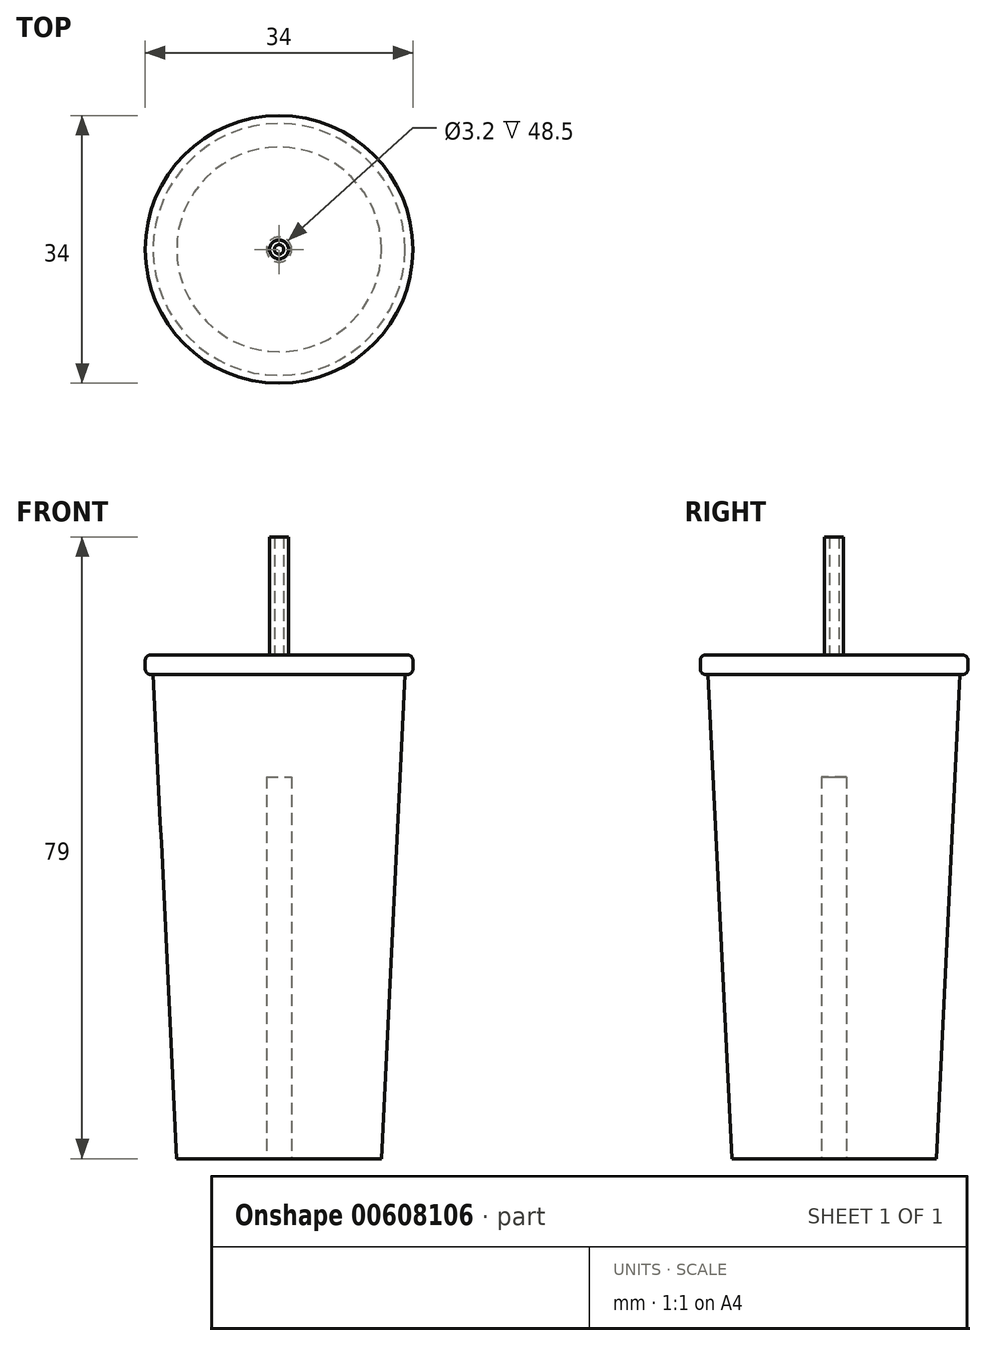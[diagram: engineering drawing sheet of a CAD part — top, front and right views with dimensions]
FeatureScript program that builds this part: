
annotation { "Feature Type Name" : "Feature", "Feature Type Description" : "" }
export const myFeature = defineFeature(function(context is Context, id is Id, definition is map)
    precondition{}
    {
        {
            var Q0;
            Q0=qCreatedBy(makeId("Front.planeOp"),FACE);
            var sketch = newSketch(context, id + "F0", { "sketchPlane" : qUnion([Q0])});
            skLineSegment(sketch, "E0", {"start": v(0, 0) * mm, "end": v(13, 0) * mm});
            skLineSegment(sketch, "E1", {"start": v(0, 0) * mm, "end": v(0, 61.5) * mm});
            skLineSegment(sketch, "E2", {"start": v(0, 61.5) * mm, "end": v(16, 61.5) * mm});
            skLineSegment(sketch, "E3", {"start": v(16, 61.5) * mm, "end": v(13, 0) * mm});
            skLineSegment(sketch, "E4", {"start": v(0, 61.5) * mm, "end": v(0, 64) * mm});
            skLineSegment(sketch, "E5", {"start": v(0, 64) * mm, "end": v(16.3, 64) * mm});
            skLineSegment(sketch, "E6", {"start": v(17, 63.3) * mm, "end": v(17, 62.2) * mm});
            skLineSegment(sketch, "E7", {"start": v(16.3, 61.5) * mm, "end": v(16, 61.5) * mm});
            skPoint(sketch, "E8.visualSharp", {"position": v(17, 64) * mm});
            skArc(sketch, "E8.filletArc", {"start": v(17, 63.3) * mm, "mid": v(16.8, 63.8) * mm, "end": v(16.3, 64) * mm});
            skPoint(sketch, "E9.visualSharp", {"position": v(17, 61.5) * mm});
            skArc(sketch, "E9.filletArc", {"start": v(16.3, 61.5) * mm, "mid": v(16.8, 61.7) * mm, "end": v(17, 62.2) * mm});
            skLineSegment(sketch, "E10", {"start": v(0, 64) * mm, "end": v(0, 79) * mm, "construction": true});
            skLineSegment(sketch, "E11", {"start": v(0, 79) * mm, "end": v(0.6, 79) * mm, "construction": true});
            skLineSegment(sketch, "E12", {"start": v(0.6, 79) * mm, "end": v(0.6, 64) * mm});
            skLineSegment(sketch, "E13", {"start": v(0.6, 79) * mm, "end": v(1.2, 79) * mm});
            skLineSegment(sketch, "E14", {"start": v(1.2, 79) * mm, "end": v(1.2, 64) * mm});
            skSolve(sketch);
        }
        {
            var Q0;
            {var subQ0=sQuery(id+"F0.wireOp",EDGE,"E12");Q0=makeQuery(id+"F0.imprint","IMPRINT",FACE,{"disambiguationData":[TD([[makeQuery(id+"F0.imprint","IMPRINT",EDGE,{"derivedFrom":subQ0}),1.0]])]});}
            var Q1;
            Q1=makeQuery(id+"F0.imprint","IMPRINT",FACE,{"disambiguationData":[TD([[makeQuery(id+"F0.imprint","IMPRINT",EDGE,{"derivedFrom":sQuery(id+"F0.wireOp",EDGE,"E2")}),1.0]])]});
            var Q2;
            Q2=makeQuery(id+"F0.imprint","IMPRINT",FACE,{"disambiguationData":[TD([[makeQuery(id+"F0.imprint","IMPRINT",EDGE,{"derivedFrom":sQuery(id+"F0.wireOp",EDGE,"E0")}),1.0]])]});
            var Q3;
            Q3=sQuery(id+"F0.wireOp",EDGE,"E10");
            revolve(context, id + "F1", {"entities" : qUnion([Q0, Q1, Q2]), "axis" : qUnion([Q3]), "revolveType" : RevolveType.FULL});
        }
        {
            var Q0;
            Q0=makeQuery(id+"F1.opRevolve","SWEPT_FACE",FACE,{"disambiguationData":[OSD([sQuery(id+"F0.wireOp",EDGE,"E0")])]});
            var sketch = newSketch(context, id + "F2", { "sketchPlane" : qUnion([Q0])});
            skCircle(sketch, "E15", {"center": v(0, 0) * mm, "radius": 1.6 * mm});
            skSolve(sketch);
        }
        {
            var Q0;
            Q0=makeQuery(id+"F2.imprint","IMPRINT",FACE,{"disambiguationData":[TD([[makeQuery(id+"F2.imprint","IMPRINT",EDGE,{"derivedFrom":sQuery(id+"F2.wireOp",EDGE,"E15")}),1.0]])]});
            extrude(context, id + "F3", {"entities" : qUnion([Q0]), "operationType" : NewBodyOperationType.REMOVE, "oppositeDirection" : true, "depth" : 48.5 * mm, "offsetDistance" : 25 * mm});
        }
    });
